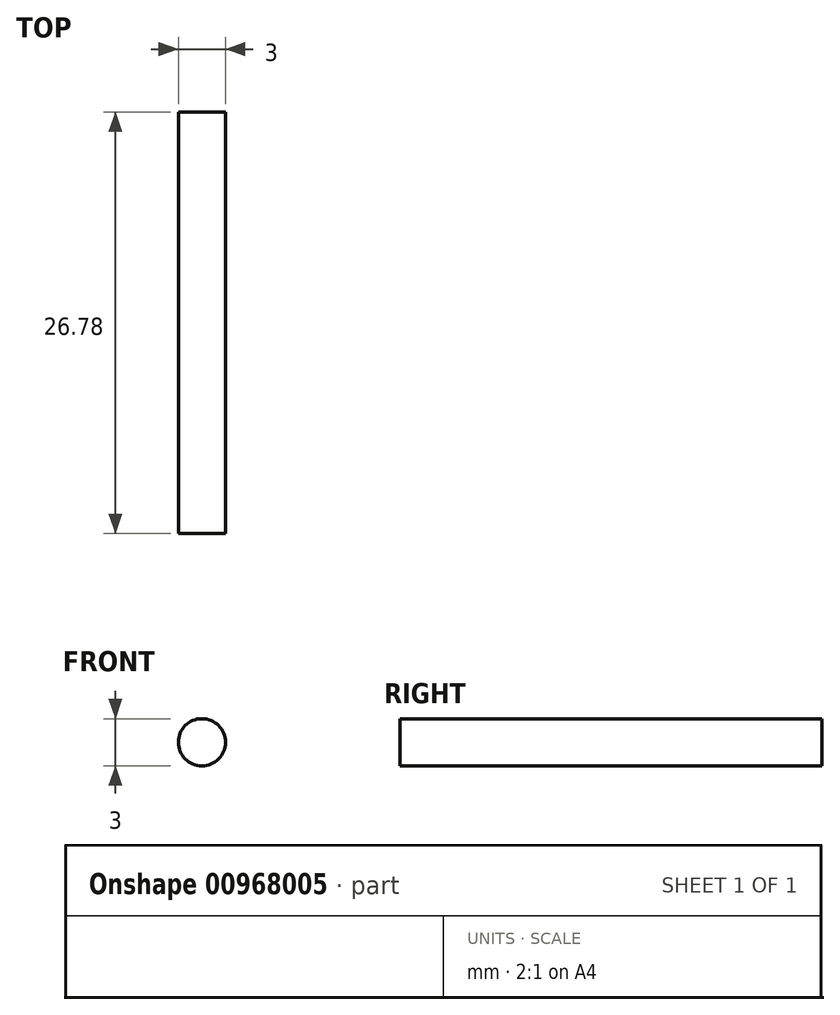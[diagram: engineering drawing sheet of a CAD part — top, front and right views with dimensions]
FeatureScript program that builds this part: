
annotation { "Feature Type Name" : "Feature", "Feature Type Description" : "" }
export const myFeature = defineFeature(function(context is Context, id is Id, definition is map)
    precondition{}
    {
        {
            var Q0;
            Q0=qCreatedBy(makeId("Front.planeOp"),FACE);
            var sketch = newSketch(context, id + "F0", { "sketchPlane" : qUnion([Q0])});
            skCircle(sketch, "E0", {"center": v(0, 0) * mm, "radius": 1.5 * mm});
            skSolve(sketch);
        }
        {
            var Q0;
            Q0=makeQuery(id+"F0.imprint","IMPRINT",FACE,{"disambiguationData":[TD([[makeQuery(id+"F0.imprint","IMPRINT",EDGE,{"derivedFrom":sQuery(id+"F0.wireOp",EDGE,"E0")}),1.0]])]});
            extrude(context, id + "F1", {"entities" : qUnion([Q0]), "oppositeDirection" : true, "depth" : 26.77 * mm, "offsetDistance" : 25 * mm});
        }
    });
